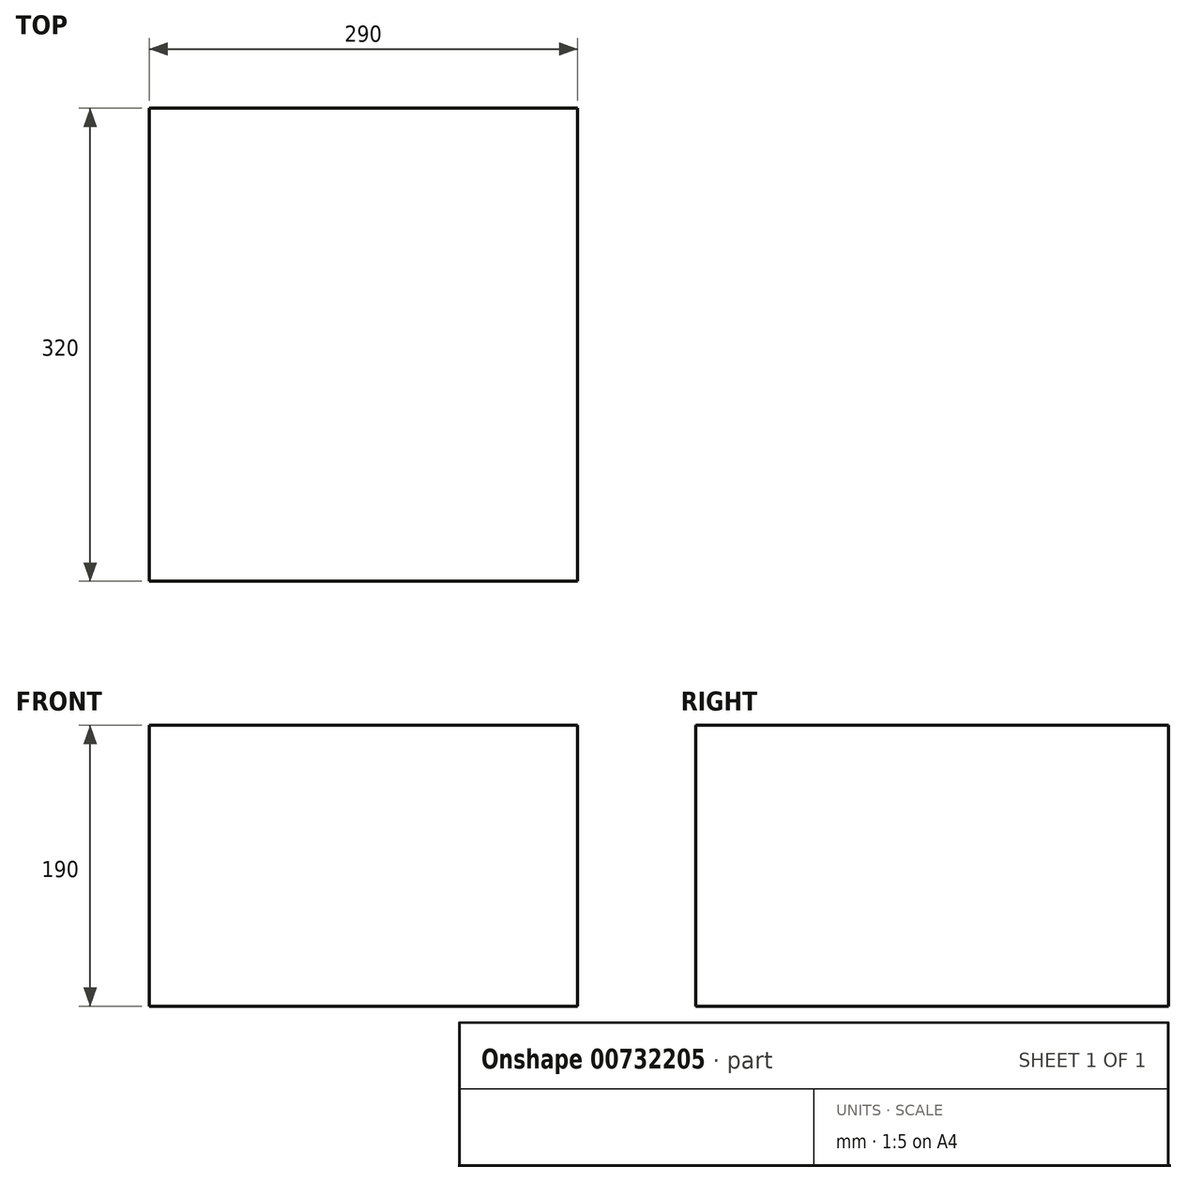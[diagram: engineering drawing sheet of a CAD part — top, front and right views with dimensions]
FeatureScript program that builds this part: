
annotation { "Feature Type Name" : "Feature", "Feature Type Description" : "" }
export const myFeature = defineFeature(function(context is Context, id is Id, definition is map)
    precondition{}
    {
        {
            var Q0;
            Q0=qCreatedBy(makeId("Top.planeOp"),FACE);
            var sketch = newSketch(context, id + "F0", { "sketchPlane" : qUnion([Q0])});
            skLineSegment(sketch, "E0.bottom", {"start": v(145, 160) * mm, "end": v(-145, 160) * mm});
            skLineSegment(sketch, "E0.top", {"start": v(145, -160) * mm, "end": v(-145, -160) * mm});
            skLineSegment(sketch, "E0.left", {"start": v(145, 160) * mm, "end": v(145, -160) * mm});
            skLineSegment(sketch, "E0.right", {"start": v(-145, 160) * mm, "end": v(-145, -160) * mm});
            skPoint(sketch, "E0.middle", {"position": v(0, 0) * mm});
            skSolve(sketch);
        }
        {
            var Q0;
            Q0 = qSketchRegion(id + "F0", true);
            extrude(context, id + "F1", {"entities" : qUnion([Q0]), "depth" : 190 * mm, "offsetDistance" : 25 * mm});
        }
    });
